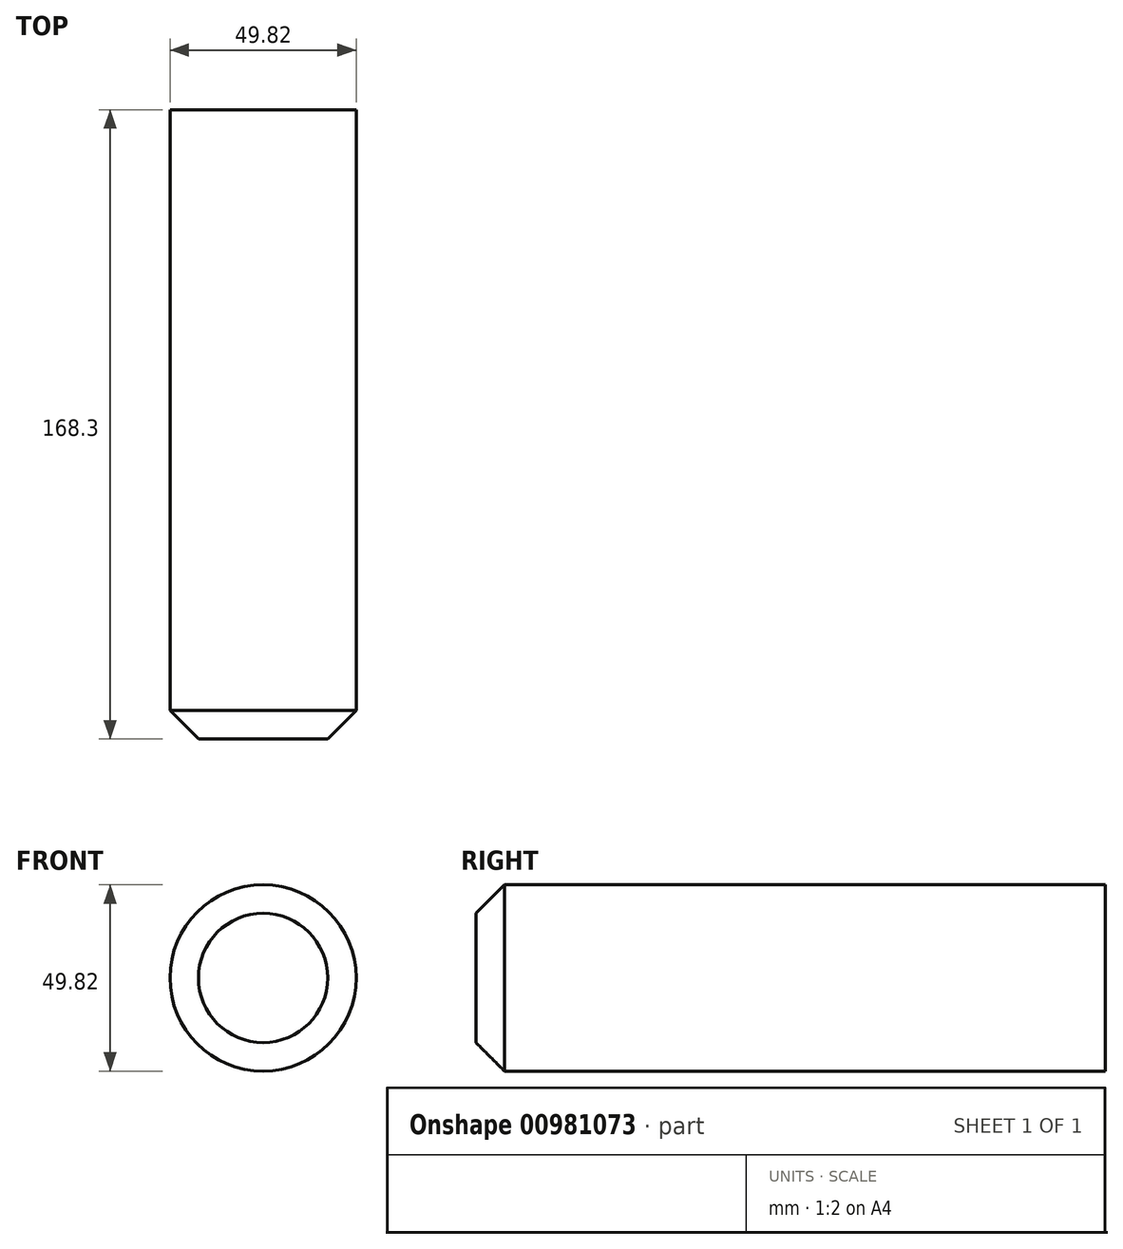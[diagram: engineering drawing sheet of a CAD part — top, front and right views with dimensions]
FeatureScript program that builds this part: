
annotation { "Feature Type Name" : "Feature", "Feature Type Description" : "" }
export const myFeature = defineFeature(function(context is Context, id is Id, definition is map)
    precondition{}
    {
        {
            var Q0;
            Q0=qCreatedBy(makeId("Front.planeOp"),FACE);
            var sketch = newSketch(context, id + "F0", { "sketchPlane" : qUnion([Q0])});
            skCircle(sketch, "E0", {"center": v(0, 0) * mm, "radius": 24.9 * mm});
            skSolve(sketch);
        }
        {
            var Q0;
            Q0=makeQuery(id+"F0.imprint","IMPRINT",FACE,{"disambiguationData":[TD([[makeQuery(id+"F0.imprint","IMPRINT",EDGE,{"derivedFrom":sQuery(id+"F0.wireOp",EDGE,"E0")}),1.0]])]});
            var Q1;
            Q1 = qSketchRegion(id + "F0", true);
            extrude(context, id + "F1", {"entities" : qUnion([Q0, Q1]), "depth" : 168.3 * mm, "offsetDistance" : 25.4 * mm});
        }
        {
            var Q0;
            Q0=makeQuery(id+"F1.opExtrude","CAP_EDGE",EDGE,{"disambiguationData":[OSD([sQuery(id+"F0.wireOp",EDGE,"E0")])],"isStart":false});
            chamfer(context, id + "F2", {"entities" : qUnion([Q0]), "width" : 7.62 * mm, "tangentPropagation" : true});
        }
    });
